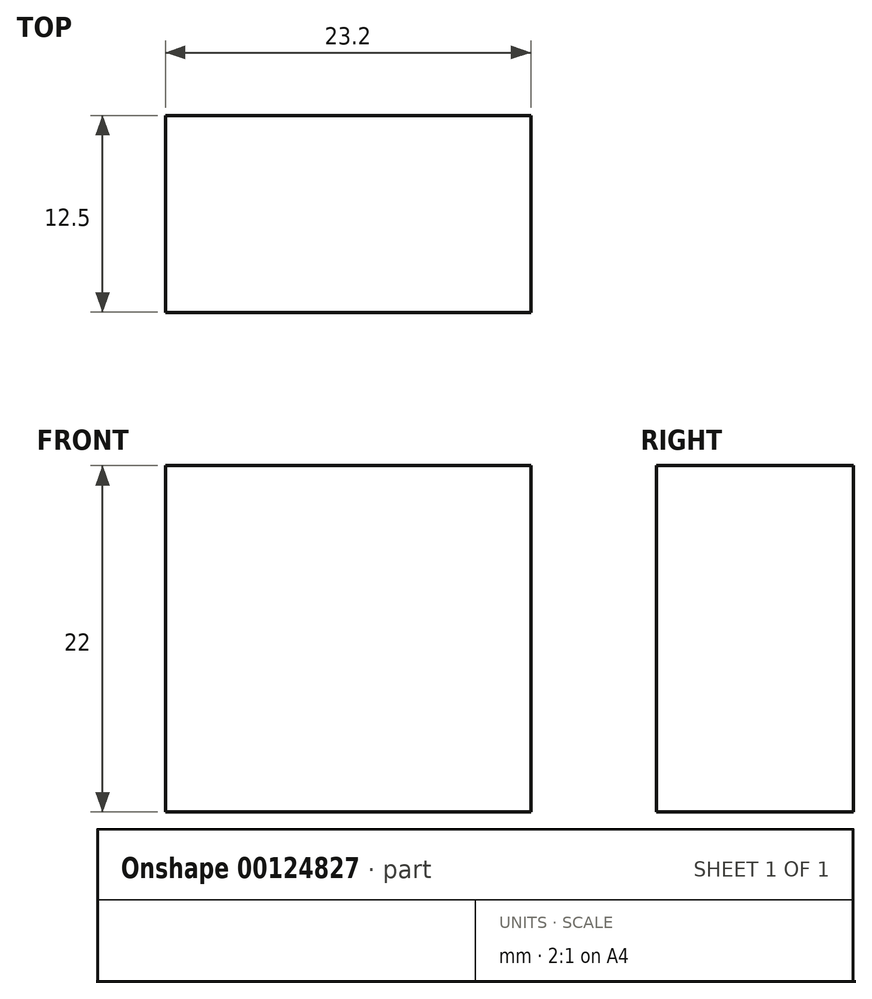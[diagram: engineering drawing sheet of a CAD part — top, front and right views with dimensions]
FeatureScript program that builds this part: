
annotation { "Feature Type Name" : "Feature", "Feature Type Description" : "" }
export const myFeature = defineFeature(function(context is Context, id is Id, definition is map)
    precondition{}
    {
        {
            var Q0;
            Q0=qCreatedBy(makeId("Top.planeOp"),FACE);
            var sketch = newSketch(context, id + "F0", { "sketchPlane" : qUnion([Q0])});
            skLineSegment(sketch, "E0.bottom", {"start": v(-13.95, 15.3) * mm, "end": v(9.25, 15.3) * mm});
            skLineSegment(sketch, "E0.top", {"start": v(-13.95, 2.8) * mm, "end": v(9.25, 2.8) * mm});
            skLineSegment(sketch, "E0.left", {"start": v(-13.95, 15.3) * mm, "end": v(-13.95, 2.8) * mm});
            skLineSegment(sketch, "E0.right", {"start": v(9.25, 15.3) * mm, "end": v(9.25, 2.8) * mm});
            skSolve(sketch);
        }
        {
            var Q0;
            Q0 = qSketchRegion(id + "F0", true);
            extrude(context, id + "F1", {"entities" : qUnion([Q0]), "depth" : 22 * mm});
        }
    });
